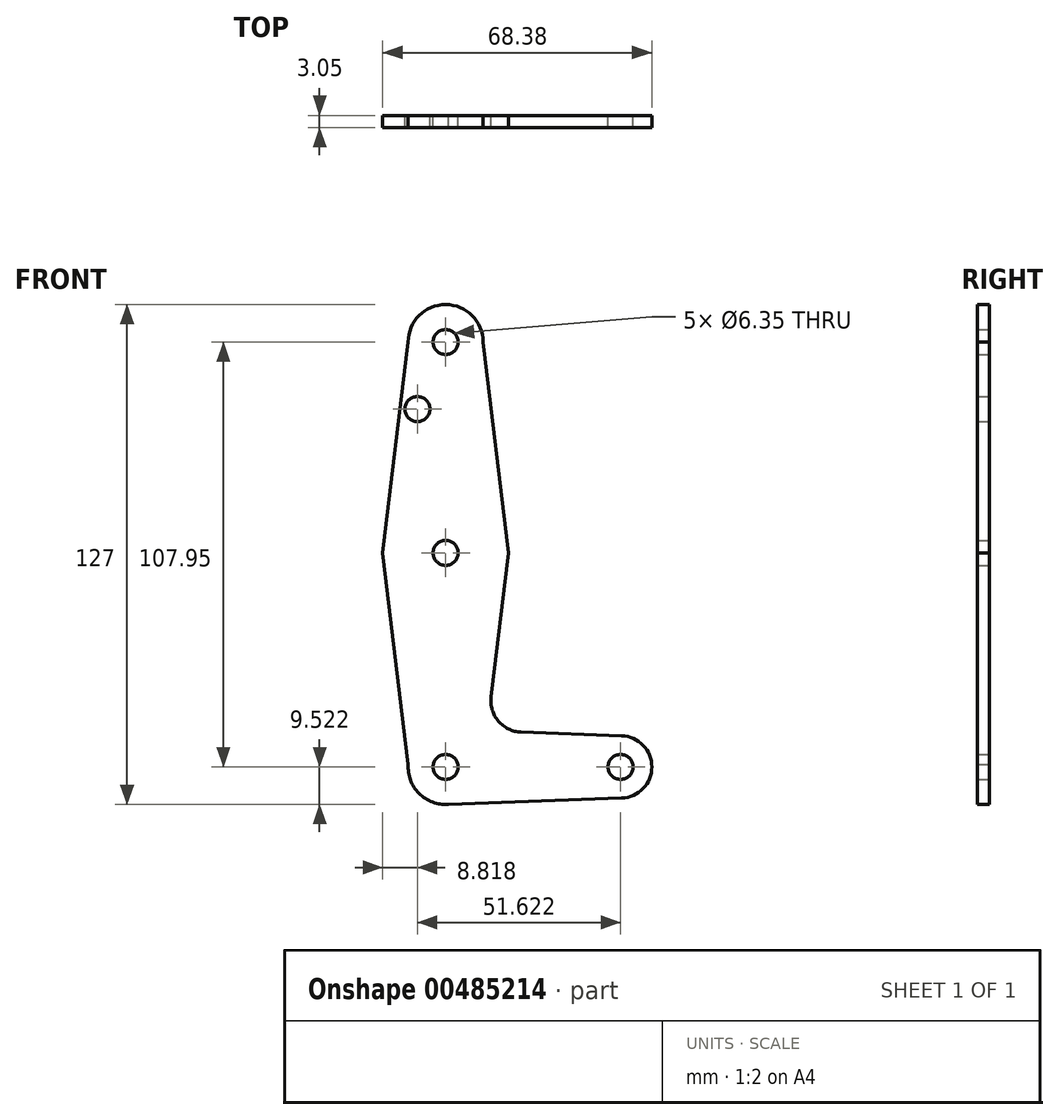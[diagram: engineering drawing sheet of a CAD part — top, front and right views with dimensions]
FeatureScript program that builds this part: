
annotation { "Feature Type Name" : "Feature", "Feature Type Description" : "" }
export const myFeature = defineFeature(function(context is Context, id is Id, definition is map)
    precondition{}
    {
        {
            var Q0;
            Q0=qCreatedBy(makeId("Front.planeOp"),FACE);
            var sketch = newSketch(context, id + "F0", { "sketchPlane" : qUnion([Q0])});
            skLineSegment(sketch, "E0", {"start": v(0, 53.55) * mm, "end": v(0, -54.4) * mm, "construction": true});
            skLineSegment(sketch, "E1", {"start": v(0, -54.4) * mm, "end": v(44.45, -54.4) * mm, "construction": true});
            skCircle(sketch, "E2", {"center": v(0, 53.55) * mm, "radius": 3.18 * mm});
            skCircle(sketch, "E3", {"center": v(0, 53.55) * mm, "radius": 9.53 * mm});
            skCircle(sketch, "E4", {"center": v(0, 0) * mm, "radius": 3.18 * mm});
            skCircle(sketch, "E5", {"center": v(0, 0) * mm, "radius": 15.88 * mm});
            skCircle(sketch, "E6", {"center": v(0, -54.4) * mm, "radius": 3.18 * mm});
            skCircle(sketch, "E7", {"center": v(0, -54.4) * mm, "radius": 9.53 * mm});
            skCircle(sketch, "E8", {"center": v(44.45, -54.4) * mm, "radius": 3.18 * mm});
            skCircle(sketch, "E9", {"center": v(44.45, -54.4) * mm, "radius": 7.94 * mm});
            skLineSegment(sketch, "E10", {"start": v(-28.69, 0) * mm, "end": v(-28.69, 36.53) * mm});
            skLineSegment(sketch, "E11", {"start": v(-28.69, 36.53) * mm, "end": v(0, 36.53) * mm});
            skCircle(sketch, "E12", {"center": v(-7.17, 36.53) * mm, "radius": 3.18 * mm});
            skLineSegment(sketch, "E13", {"start": v(-28.69, 0) * mm, "end": v(-28.69, -63.5) * mm});
            skLineSegment(sketch, "E14", {"start": v(0, 15.87) * mm, "end": v(0, 40.12) * mm});
            skLineSegment(sketch, "E15", {"start": v(0, 15.87) * mm, "end": v(0, 44.03) * mm});
            skLineSegment(sketch, "E16", {"start": v(0, 53.55) * mm, "end": v(0, 21.8) * mm, "construction": true});
            skLineSegment(sketch, "E17", {"start": v(0, 0) * mm, "end": v(0, 36.53) * mm});
            skLineSegment(sketch, "E18", {"start": v(-9.52, 53.55) * mm, "end": v(-16, 0) * mm});
            skLineSegment(sketch, "E19", {"start": v(-16, 0) * mm, "end": v(-9.5, -53.74) * mm});
            skLineSegment(sketch, "E20", {"start": v(9.52, 53.55) * mm, "end": v(16, 0) * mm});
            skLineSegment(sketch, "E21", {"start": v(16, 0) * mm, "end": v(11.56, -36.66) * mm});
            skLineSegment(sketch, "E22", {"start": v(19.17, -45.56) * mm, "end": v(44.73, -46.47) * mm});
            skLineSegment(sketch, "E23", {"start": v(0, -63.92) * mm, "end": v(44.73, -62.33) * mm});
            skLineSegment(sketch, "E24", {"start": v(16, 0) * mm, "end": v(11.28, -39.02) * mm});
            skLineSegment(sketch, "E25", {"start": v(44.73, -46.47) * mm, "end": v(16, -45.44) * mm});
            skPoint(sketch, "E26.newPointA", {"position": v(0, -44.87) * mm});
            skPoint(sketch, "E26.newPointB", {"position": v(9.5, -53.74) * mm});
            skArc(sketch, "E26.filletArc", {"start": v(11.56, -36.66) * mm, "mid": v(13.42, -42.78) * mm, "end": v(19.17, -45.56) * mm});
            skSolve(sketch);
        }
        {
            var Q0;
            Q0 = qSketchRegion(id + "F0", true);
            extrude(context, id + "F1", {"entities" : qUnion([Q0]), "depth" : 3.05 * mm});
        }
    });
